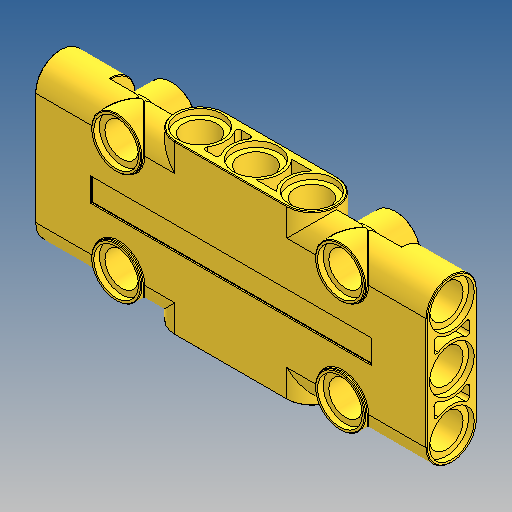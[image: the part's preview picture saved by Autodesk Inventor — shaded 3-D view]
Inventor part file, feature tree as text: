
AUTODESK INVENTOR PART (.ipt)
format: ipt  version: 2025 (Build 290162010, 162A)  size: 1,119,232 bytes
history: native  units: in
note: dims shown in document units (in); Inventor stores cm internally (conversion verified against a paired STEP export)
features: extrude x16, sketch x11, mirror x3, plane x1, fillet x1
ambient origin geometry x8: Origin, YZ Plane, XZ Plane, XY Plane, X Axis, Y Axis, Z Axis, Center Point
bodies: Solid1 (feature_tree)
feature tree (32):
  extrude  "Extrusion1"  Depth=0.189in
  sketch  "Sketch3"  dims[d4=2.2047in d5=0.0in]
  extrude  "Extrusion2"  Depth=0.0315in
  extrude  "Extrusion3"  TaperAngle=0.0deg  [1 undecoded]
  extrude  "Extrusion4"  Depth=0.252in
  plane  "Work Plane1"
  extrude  "Extrusion5"  Depth=0.315in
  sketch  "Sketch5"  dims[d12=0.3937in d14=0.3937in d16=0.2835in]
  extrude  "Extrusion6"  Depth=0.2835in
  extrude  "Extrusion7"  Depth=0.0315in
  extrude  "Extrusion10"  Depth=0.2205in TaperAngle=0.0deg
  extrude  "Extrusion8"  Depth=0.189in
  extrude  "Extrusion9"  Depth=0.0315in TaperAngle=0.0deg
  mirror  "Mirror1"
  mirror  "Mirror2"
  sketch  "Sketch8"  dims[d22=-0.1417in d23=0.189in]
  extrude  "Extrusion11"  Depth=0.189in
  extrude  "Extrusion12"  Depth=0.3937in
  extrude  "Extrusion13"  Depth=0.2677in
  sketch  "Sketch9"  dims[d24=0.2835in d25=0.0315in d26=0.0in]
  extrude  "Extrusion14"  TaperAngle=0.0deg  [1 undecoded]
  extrude  "Extrusion16"  Depth=0.2677in TaperAngle=0.0deg
  mirror  "Mirror3"
  extrude  "Extrusion15"  Depth=0.252in
  fillet  "Fillet1"  Radius=0.0315in
  sketch  "Sketch2"  dims[d2=0.2835in d3=0.0315in]
  sketch  "Skizze - Rechteckige Anordnung1"  dims[d0=0.315in d1=0.189in]
  sketch  "Sketch4"  dims[d8=45.0deg d9=0.7874in d11=0.315in]
  sketch  "Sketch6"  dims[d17=0.0in d18=0.0315in]
  sketch  "Sketch7"  dims[d19=0.0in d20=0.2205in d21=0.0in]
  sketch  "Sketch10"  dims[d27=0.2835in d28=0.189in d29=0.6299in d30=0.2677in d31=0.0472in d32=0.0in d33=0.0in d34=0.2677in d35=0.0in d36=0.252in d37=0.0315in d38=0.0in d39=0.252in d40=0.0315in d41=0.0in d42=0.0315in d43=0.2205in d44=0.0in d45=0.2835in d46=0.6299in d47=0.189in d48=0.1417in d49=0.1417in d50=0.0in d51=0.0in d52=0.1417in d53=0.0in d54=0.315in d55=0.0in d56=0.252in d57=0.0315in d58=0.0in d59=1.5748in d60=0.126in d62=0.0079in d63=0.0in d64=45.0deg d72=0.2205in d73=0.0in d74=0.0039in d75=0.0157in d76=0.7874in d78=0.315in d79=0.3937in d81=0.3937in]
  sketch  "Skizze - Rechteckige Anordnung3"  dims[d6=0.189in d7=0.252in]
note: 2 required parameter values undecoded (feature->parameter linkage not recoverable at this tier; creation-order binding heuristic only, values carry confidence <= 0.55)
